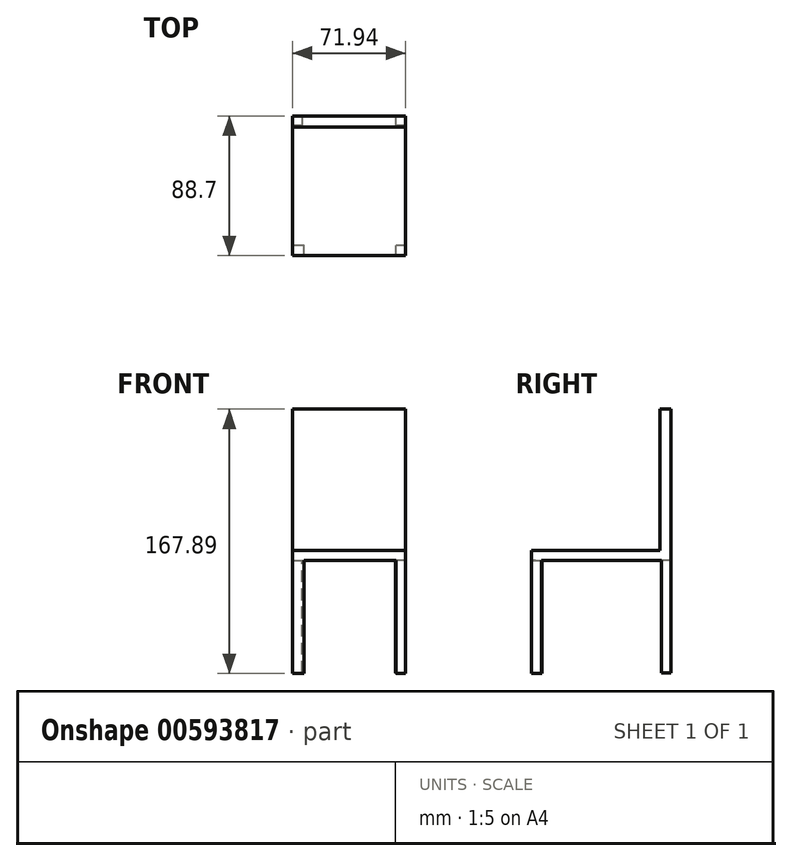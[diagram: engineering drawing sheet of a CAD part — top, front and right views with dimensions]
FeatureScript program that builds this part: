
annotation { "Feature Type Name" : "Feature", "Feature Type Description" : "" }
export const myFeature = defineFeature(function(context is Context, id is Id, definition is map)
    precondition{}
    {
        {
            var Q0;
            Q0=qCreatedBy(makeId("Top.planeOp"),FACE);
            var sketch = newSketch(context, id + "F0", { "sketchPlane" : qUnion([Q0])});
            skLineSegment(sketch, "E0.bottom", {"start": v(-37.95, 44.2) * mm, "end": v(33.99, 44.2) * mm});
            skLineSegment(sketch, "E0.top", {"start": v(-37.95, -44.5) * mm, "end": v(33.99, -44.5) * mm});
            skLineSegment(sketch, "E0.left", {"start": v(-37.95, 44.2) * mm, "end": v(-37.95, -44.5) * mm});
            skLineSegment(sketch, "E0.right", {"start": v(33.99, 44.2) * mm, "end": v(33.99, -44.5) * mm});
            skSolve(sketch);
        }
        {
            var Q0;
            Q0=makeQuery(id+"F0.imprint","IMPRINT",FACE,{"disambiguationData":[TD([[makeQuery(id+"F0.imprint","IMPRINT",EDGE,{"derivedFrom":sQuery(id+"F0.wireOp",EDGE,"E0.bottom")}),-1.0]])]});
            extrude(context, id + "F1", {"entities" : qUnion([Q0]), "depth" : 6.35 * mm, "offsetDistance" : 25.4 * mm});
        }
        {
            var Q0;
            Q0=qCreatedBy(makeId("Top.planeOp"),FACE);
            var sketch = newSketch(context, id + "F2", { "sketchPlane" : qUnion([Q0])});
            skLineSegment(sketch, "E1.bottom", {"start": v(-37.64, -44.5) * mm, "end": v(-30.63, -44.5) * mm});
            skLineSegment(sketch, "E1.top", {"start": v(-37.64, -37.8) * mm, "end": v(-30.63, -37.8) * mm});
            skLineSegment(sketch, "E1.left", {"start": v(-37.64, -44.5) * mm, "end": v(-37.64, -37.8) * mm});
            skLineSegment(sketch, "E1.right", {"start": v(-30.63, -44.5) * mm, "end": v(-30.63, -37.8) * mm});
            skLineSegment(sketch, "E2.bottom", {"start": v(33.68, -44.5) * mm, "end": v(27.28, -44.5) * mm});
            skLineSegment(sketch, "E2.top", {"start": v(33.68, -37.8) * mm, "end": v(27.28, -37.8) * mm});
            skLineSegment(sketch, "E2.left", {"start": v(33.68, -44.5) * mm, "end": v(33.68, -37.8) * mm});
            skLineSegment(sketch, "E2.right", {"start": v(27.28, -44.5) * mm, "end": v(27.28, -37.8) * mm});
            skSolve(sketch);
        }
        {
            var Q0;
            Q0=makeQuery(id+"F2.imprint","IMPRINT",FACE,{"disambiguationData":[TD([[makeQuery(id+"F2.imprint","IMPRINT",EDGE,{"derivedFrom":sQuery(id+"F2.wireOp",EDGE,"E1.bottom")}),1.0]])]});
            extrude(context, id + "F3", {"entities" : qUnion([Q0]), "operationType" : NewBodyOperationType.ADD, "oppositeDirection" : true, "depth" : 71.88 * mm, "offsetDistance" : 25.4 * mm});
        }
        {
            var Q0;
            Q0=qCreatedBy(makeId("Top.planeOp"),FACE);
            var sketch = newSketch(context, id + "F4", { "sketchPlane" : qUnion([Q0])});
            skLineSegment(sketch, "E3.bottom", {"start": v(33.99, -44.5) * mm, "end": v(27.89, -44.5) * mm});
            skLineSegment(sketch, "E3.top", {"start": v(33.99, -38.1) * mm, "end": v(27.89, -38.1) * mm});
            skLineSegment(sketch, "E3.left", {"start": v(33.99, -44.5) * mm, "end": v(33.99, -38.1) * mm});
            skLineSegment(sketch, "E3.right", {"start": v(27.89, -44.5) * mm, "end": v(27.89, -38.1) * mm});
            skSolve(sketch);
        }
        {
            var Q0;
            Q0=makeQuery(id+"F4.imprint","IMPRINT",FACE,{"disambiguationData":[TD([[makeQuery(id+"F4.imprint","IMPRINT",EDGE,{"derivedFrom":sQuery(id+"F4.wireOp",EDGE,"E3.bottom")}),-1.0]])]});
            extrude(context, id + "F5", {"entities" : qUnion([Q0]), "operationType" : NewBodyOperationType.ADD, "oppositeDirection" : true, "depth" : 71.88 * mm, "offsetDistance" : 25.4 * mm});
        }
        {
            var Q0;
            Q0=makeQuery(id+"F1.opExtrude","CAP_FACE",FACE,{"disambiguationData":[OSD([sQuery(id+"F0.wireOp",EDGE,"E0.bottom"),sQuery(id+"F0.wireOp",EDGE,"E0.top"),sQuery(id+"F0.wireOp",EDGE,"E0.left"),sQuery(id+"F0.wireOp",EDGE,"E0.right")])],"isStart":true});
            var sketch = newSketch(context, id + "F6", { "sketchPlane" : qUnion([Q0])});
            skLineSegment(sketch, "E4.bottom", {"start": v(-37.95, -44.2) * mm, "end": v(-31.85, -44.2) * mm});
            skLineSegment(sketch, "E4.top", {"start": v(-37.95, -38.4) * mm, "end": v(-31.85, -38.4) * mm});
            skLineSegment(sketch, "E4.left", {"start": v(-37.95, -44.2) * mm, "end": v(-37.95, -38.4) * mm});
            skLineSegment(sketch, "E4.right", {"start": v(-31.85, -44.2) * mm, "end": v(-31.85, -38.4) * mm});
            skSolve(sketch);
        }
        {
            var Q0;
            Q0=makeQuery(id+"F6.imprint","IMPRINT",FACE,{"disambiguationData":[TD([[makeQuery(id+"F6.imprint","IMPRINT",EDGE,{"derivedFrom":sQuery(id+"F6.wireOp",EDGE,"E4.bottom")}),1.0]])]});
            extrude(context, id + "F7", {"entities" : qUnion([Q0]), "operationType" : NewBodyOperationType.ADD, "depth" : 71.37 * mm, "offsetDistance" : 25.4 * mm});
        }
        {
            var Q0;
            Q0=makeQuery(id+"F1.opExtrude","CAP_FACE",FACE,{"disambiguationData":[OSD([sQuery(id+"F0.wireOp",EDGE,"E0.bottom"),sQuery(id+"F0.wireOp",EDGE,"E0.top"),sQuery(id+"F0.wireOp",EDGE,"E0.left"),sQuery(id+"F0.wireOp",EDGE,"E0.right")])],"isStart":true});
            var sketch = newSketch(context, id + "F8", { "sketchPlane" : qUnion([Q0])});
            skLineSegment(sketch, "E5.bottom", {"start": v(33.99, -44.2) * mm, "end": v(27.58, -44.2) * mm});
            skLineSegment(sketch, "E5.top", {"start": v(33.99, -38.1) * mm, "end": v(27.58, -38.1) * mm});
            skLineSegment(sketch, "E5.left", {"start": v(33.99, -44.2) * mm, "end": v(33.99, -38.1) * mm});
            skLineSegment(sketch, "E5.right", {"start": v(27.58, -44.2) * mm, "end": v(27.58, -38.1) * mm});
            skSolve(sketch);
        }
        {
            var Q0;
            Q0 = qSketchRegion(id + "F8", true);
            extrude(context, id + "F9", {"entities" : qUnion([Q0]), "operationType" : NewBodyOperationType.ADD, "depth" : 71.63 * mm, "offsetDistance" : 25.4 * mm});
        }
        {
            var Q0;
            Q0=makeQuery(id+"F1.opExtrude","CAP_FACE",FACE,{"disambiguationData":[OSD([sQuery(id+"F0.wireOp",EDGE,"E0.bottom"),sQuery(id+"F0.wireOp",EDGE,"E0.top"),sQuery(id+"F0.wireOp",EDGE,"E0.left"),sQuery(id+"F0.wireOp",EDGE,"E0.right")])],"isStart":false});
            var sketch = newSketch(context, id + "F10", { "sketchPlane" : qUnion([Q0])});
            skLineSegment(sketch, "E6.bottom", {"start": v(-37.95, 44.2) * mm, "end": v(33.99, 44.2) * mm});
            skLineSegment(sketch, "E6.top", {"start": v(-37.95, 37.1) * mm, "end": v(33.99, 37.1) * mm});
            skLineSegment(sketch, "E6.left", {"start": v(-37.95, 44.2) * mm, "end": v(-37.95, 37.1) * mm});
            skLineSegment(sketch, "E6.right", {"start": v(33.99, 44.2) * mm, "end": v(33.99, 37.1) * mm});
            skSolve(sketch);
        }
        {
            var Q0;
            Q0 = qSketchRegion(id + "F10", true);
            extrude(context, id + "F11", {"entities" : qUnion([Q0]), "operationType" : NewBodyOperationType.ADD, "depth" : 89.66 * mm, "offsetDistance" : 25.4 * mm});
        }
    });
